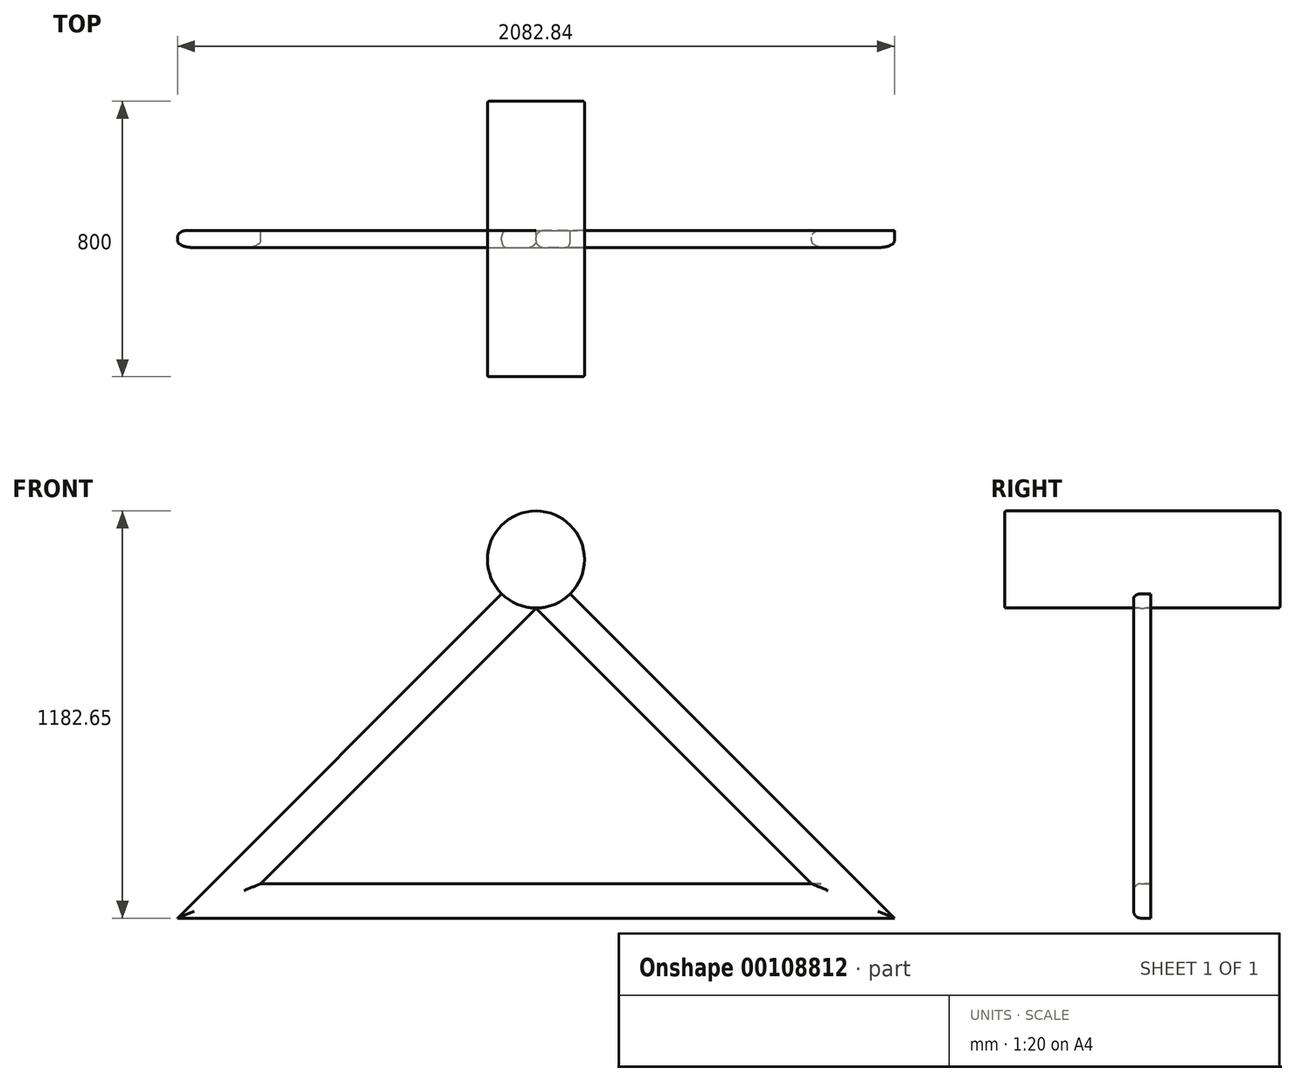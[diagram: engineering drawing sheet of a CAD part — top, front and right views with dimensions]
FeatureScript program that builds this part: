
annotation { "Feature Type Name" : "Feature", "Feature Type Description" : "" }
export const myFeature = defineFeature(function(context is Context, id is Id, definition is map)
    precondition{}
    {
        {
            var Q0;
            Q0=qCreatedBy(makeId("Front.planeOp"),FACE);
            var sketch = newSketch(context, id + "F0", { "sketchPlane" : qUnion([Q0])});
            skLineSegment(sketch, "E0", {"start": v(0, 0) * mm, "end": v(0, 0) * mm});
            skLineSegment(sketch, "E1", {"start": v(0, 0) * mm, "end": v(0, 800) * mm, "construction": true});
            skLineSegment(sketch, "E2", {"start": v(0, 0) * mm, "end": v(800, 0) * mm});
            skLineSegment(sketch, "E3", {"start": v(0, 0) * mm, "end": v(-800, 0) * mm});
            skLineSegment(sketch, "E4", {"start": v(-800, 0) * mm, "end": v(0, 800) * mm});
            skLineSegment(sketch, "E5", {"start": v(800, 0) * mm, "end": v(0, 800) * mm});
            skLineSegment(sketch, "E6.0", {"start": v(1041.42, -100) * mm, "end": v(0, 941.42) * mm});
            skLineSegment(sketch, "E6.1", {"start": v(0, -100) * mm, "end": v(1041.42, -100) * mm});
            skLineSegment(sketch, "E6.2", {"start": v(0, -100) * mm, "end": v(-1041.42, -100) * mm});
            skLineSegment(sketch, "E6.3", {"start": v(-1041.42, -100) * mm, "end": v(0, 941.42) * mm});
            skSolve(sketch);
        }
        {
            var Q0;
            Q0=makeQuery(id+"F0.imprint","IMPRINT",FACE,{"disambiguationData":[TD([[makeQuery(id+"F0.imprint","IMPRINT",EDGE,{"derivedFrom":sQuery(id+"F0.wireOp",EDGE,"E2")}),1.0]])]});
            var sketch = newSketch(context, id + "F1", { "sketchPlane" : qUnion([Q0])});
            skCircle(sketch, "E7", {"center": v(0, 941.67) * mm, "radius": 140.98 * mm});
            skSolve(sketch);
        }
        {
            var Q0;
            Q0 = qSketchRegion(id + "F1", true);
            extrude(context, id + "F2", {"entities" : qUnion([Q0]), "endBound" : BoundingType.SYMMETRIC, "depth" : 800 * mm});
        }
        {
            var Q0;
            Q0=makeQuery(id+"F0.imprint","IMPRINT",FACE,{"disambiguationData":[TD([[makeQuery(id+"F0.imprint","IMPRINT",EDGE,{"derivedFrom":sQuery(id+"F0.wireOp",EDGE,"E2")}),-1.0]])]});
            extrude(context, id + "F3", {"entities" : qUnion([Q0]), "operationType" : NewBodyOperationType.ADD, "endBound" : BoundingType.SYMMETRIC, "depth" : 50 * mm});
        }
        {
            var Q0;
            Q0=makeQuery(id+"F3.opExtrude","CAP_EDGE",EDGE,{"disambiguationData":[OSD([sQuery(id+"F0.wireOp",EDGE,"E6.3")])],"isStart":false});
            var Q1;
            Q1=makeQuery(id+"F3.opExtrude","CAP_EDGE",EDGE,{"disambiguationData":[OSD([sQuery(id+"F0.wireOp",EDGE,"E4")])],"isStart":false});
            var Q2;
            Q2=makeQuery(id+"F3.opExtrude","CAP_EDGE",EDGE,{"disambiguationData":[OSD([sQuery(id+"F0.wireOp",EDGE,"E6.3")])],"isStart":true});
            var Q3;
            Q3=makeQuery(id+"F3.opExtrude","CAP_EDGE",EDGE,{"disambiguationData":[OSD([sQuery(id+"F0.wireOp",EDGE,"E2"),sQuery(id+"F0.wireOp",EDGE,"E3")])],"isStart":false});
            var Q4;
            Q4=makeQuery(id+"F3.opExtrude","CAP_EDGE",EDGE,{"disambiguationData":[OSD([sQuery(id+"F0.wireOp",EDGE,"E6.1"),sQuery(id+"F0.wireOp",EDGE,"E6.2")])],"isStart":false});
            var Q5;
            Q5=makeQuery(id+"F3.opExtrude","CAP_EDGE",EDGE,{"disambiguationData":[OSD([sQuery(id+"F0.wireOp",EDGE,"E5")])],"isStart":false});
            var Q6;
            Q6=makeQuery(id+"F3.opExtrude","CAP_EDGE",EDGE,{"disambiguationData":[OSD([sQuery(id+"F0.wireOp",EDGE,"E5")])],"isStart":true});
            var Q7;
            Q7=makeQuery(id+"F3.opExtrude","CAP_EDGE",EDGE,{"disambiguationData":[OSD([sQuery(id+"F0.wireOp",EDGE,"E6.0")])],"isStart":false});
            fillet(context, id + "F4", {"entities" : qUnion([Q0, Q1, Q2, Q3, Q4, Q5, Q6, Q7]), "radius" : 20 * mm, "tangentPropagation" : true, "allowEdgeOverflow" : false});
        }
        {
            var Q0;
            Q0=makeQuery(id+"F2.opExtrude","CAP_EDGE",EDGE,{"disambiguationData":[OSD([sQuery(id+"F1.wireOp",EDGE,"E7")])],"isStart":true});
            var Q1;
            Q1=makeQuery(id+"F2.opExtrude","CAP_EDGE",EDGE,{"disambiguationData":[OSD([sQuery(id+"F1.wireOp",EDGE,"E7")])],"isStart":false});
            fillet(context, id + "F5", {"entities" : qUnion([Q0, Q1]), "radius" : 5 * mm, "tangentPropagation" : true, "allowEdgeOverflow" : false});
        }
    });
